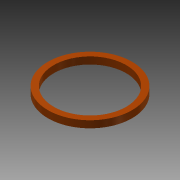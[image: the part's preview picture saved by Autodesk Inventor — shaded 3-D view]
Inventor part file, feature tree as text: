
AUTODESK INVENTOR PART (.ipt)
format: ipt  version: 2013 (Build 170138000, 138)  size: 74,752 bytes
history: native  units: mm
features: extrude x1, sketch x1
ambient origin geometry x8: Origin, YZ Plane, XZ Plane, XY Plane, X Axis, Y Axis, Z Axis, Center Point
bodies: Solid1 (feature_tree)
feature tree (2):
  extrude  "Extrusion1"  Depth=18.0mm
  sketch  "Sketch1"  dims[d0=15.5mm d2=18.0mm d3=1.5mm d4=0.0mm]
